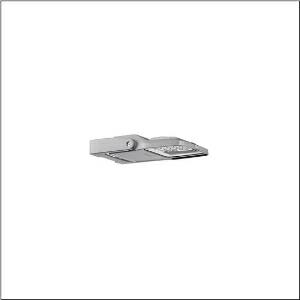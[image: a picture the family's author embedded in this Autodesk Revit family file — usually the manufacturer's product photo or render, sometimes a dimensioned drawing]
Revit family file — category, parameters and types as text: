
# Revit family: floodlight_fl_21_micro___pl61_5xa7761a2c2a_1840
name_source: partatom
category: Lighting Fixtures
units: mm (PartAtom-declared; Revit-internal decimal feet)

## family parameters
Cut with Voids When Loaded = No
Host = Face
Light Source = No
Part Type = Normal
Room Calculation Point = No
Round Connector Dimension = Use Diameter
Shared = No

## types (1)
- --- (1 x LED, 2910 lm, 23.1 W, 3000K)
    Apparent Load = 23 VA
    CIE Flux Codes = 33 65 98 100 100
    Color Rendering = 70
    Color Temperature = 3000K
    Default Elevation = 1800 mm
    Description = Floodlight FL 21 micro, floodlight, primary light control with lens, of PMMA, primary optical cover: protective disc, of toughened safety glass, transparent, light distribution: PL61, light emission: direct distribution, installation type: surface-mounted, LED, High Power LED, rated luminous flux: 2.910lm, luminous efficacy: 126lm/W, light colour: 730, colour temperature: 3000K, control gear: ECG iQ, control: optimised constant luminous flux control (CLO 2.0), Desk-Remote (wireless, voltage-free reading and setting of iQ features in the workshop via application-optimized NFC function/RFID function), Light-Fading, Smart-Wire, Night-Set, Lumen-Switch, Temp-Guard, Auto-Match, with terminal, 6-pole, mains connection: 220..240V, AC, 50/60Hz, start of lifetime: 23W, end of lifetime: 24W, reduction: 11W, luminaire housing, of diecast aluminium, powder-coated, Siteco® metallic grey (DB 702S), corrosivity category C5 according to DIN EN ISO 12944, design bracket, of diecast aluminium, powder-coated, Siteco® metallic grey (DB 702S), protection rating (complete): IP66, insulation class (complete): insulation class II (safety insulation), certification: CE, protection symbol: D, impact resistance: IK07, permissible operating ambient temperature: -40..+40°C, permissible operating ambient temperature for outdoor applications: -40..+50°C, standard: DIN EN 12944, packaging unit: 1 piece

Light Distribution: PL61
    Height = 65 mm
    Lamp = 1 x LED
    Lamp Light Flux = 2910 lm
    Lamp Power = 23.1 W
    Lamp count = 1
    Length = 312 mm
    Luminous efficacy = 126 lm/W
    Manufacturer = Siteco
    ModVariant = No
    Model = 5XA7761A2C2A
    Number of Poles = 1
    OnlyDefault = Yes
    Power Factor = 1
    Product Name = Floodlight FL 21 micro | PL61
    Product group = floodlight | pylon top
    ProductGroupID = 6101
    Protection Class = Protection class II
    Protection Degree = IP 66
    RLX_Detail_Level = 1
    RlxData = <blob elided: 97589 chars, md5=6ddaf905>
    Socket = socket
    Standby Power = 0 W
    System Light Flux = 2910 lm
    System Power = 23 W
    Type Comments = factory setting: luminous flux: 100 % | dim-lin: 254 | 455 mA
    Type Image = l_1006878.jpg
    URL = http://relux.com
    VarID = @adj_115579
    Voltage = 0 V
    Weight = 0.00 kg
    Width = 230 mm

## geometry (parser evidence)
native form markers: Blend x4, Sweep x14
no freeform markers — native parametric forms only
